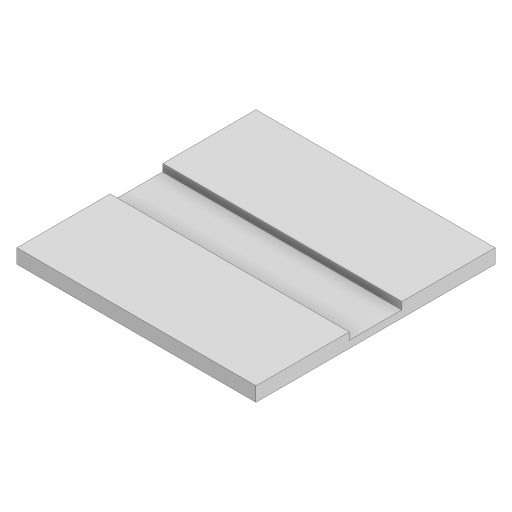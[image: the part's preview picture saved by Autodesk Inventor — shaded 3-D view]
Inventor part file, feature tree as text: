
AUTODESK INVENTOR PART (.ipt)
format: ipt  version: 2023 (Build 270158000, 158)  size: 122,880 bytes
history: native  units: in
note: dims shown in document units (in); Inventor stores cm internally (conversion verified against a paired STEP export)
features: extrude x3, sketch x3, projected_geometry x2
ambient origin geometry x8: Origin, YZ Plane, XZ Plane, XY Plane, X Axis, Y Axis, Z Axis, Center Point
bodies: Solid1 (feature_tree)
feature tree (8):
  extrude  "Extrusion1"  Depth=3937.0079in
  extrude  "Extrusion2"  Depth=118.1102in TaperAngle=0.0deg
  extrude  "Extrusion3"  Depth=1.0in TaperAngle=0.0deg
  sketch  "Sketch1"  dims[d0=3937.0079in d1=3937.0079in]
  sketch  "Sketch2"  dims[d2=118.1102in d3=0.0in d4=118.1102in d5=0.0in]
  projected_geometry  "Projected Loop1"
  sketch  "Sketch3"  dims[d6=7874.0157in d7=1.0in d8=0.0in]
  projected_geometry  "Projected Loop2"
